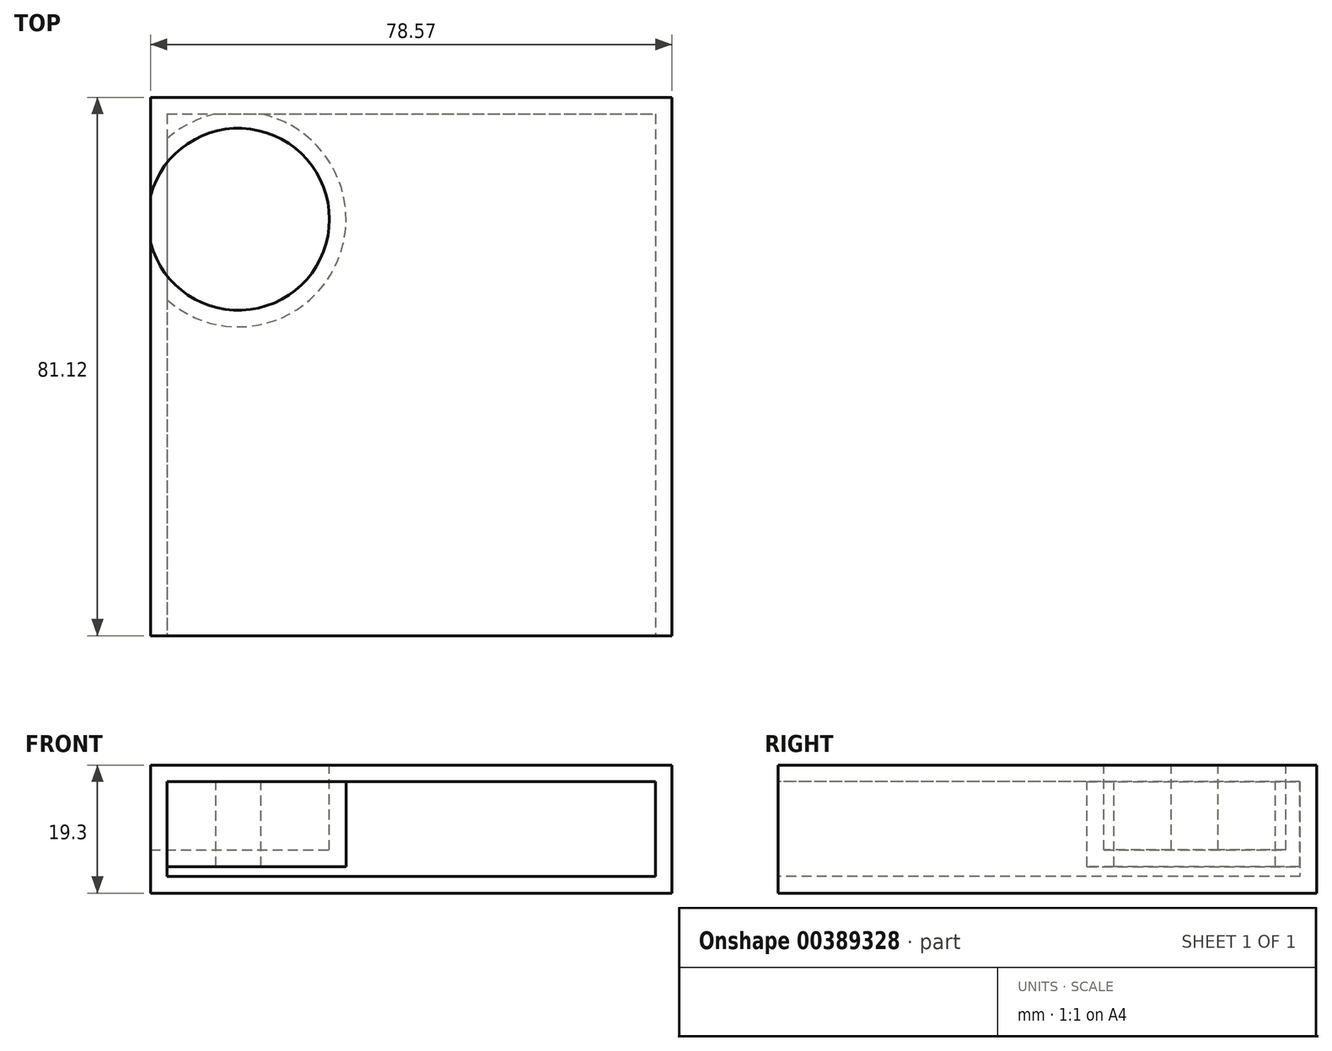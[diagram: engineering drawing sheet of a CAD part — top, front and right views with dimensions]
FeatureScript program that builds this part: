
annotation { "Feature Type Name" : "Feature", "Feature Type Description" : "" }
export const myFeature = defineFeature(function(context is Context, id is Id, definition is map)
    precondition{}
    {
        {
            var Q0;
            Q0=qCreatedBy(makeId("Top.planeOp"),FACE);
            var sketch = newSketch(context, id + "F0", { "sketchPlane" : qUnion([Q0])});
            skLineSegment(sketch, "E0.bottom", {"start": v(-38.35, 36.63) * mm, "end": v(40.22, 36.63) * mm});
            skLineSegment(sketch, "E0.top", {"start": v(-38.35, -33.82) * mm, "end": v(40.22, -33.82) * mm});
            skLineSegment(sketch, "E0.left", {"start": v(-38.35, 36.63) * mm, "end": v(-38.35, -33.82) * mm});
            skLineSegment(sketch, "E0.right", {"start": v(40.22, 36.63) * mm, "end": v(40.22, -33.82) * mm});
            skSolve(sketch);
        }
        {
            var Q0;
            Q0=makeQuery(id+"F0.imprint","IMPRINT",FACE,{"disambiguationData":[TD([[makeQuery(id+"F0.imprint","IMPRINT",EDGE,{"derivedFrom":sQuery(id+"F0.wireOp",EDGE,"E0.bottom")}),-1.0]])]});
            extrude(context, id + "F1", {"entities" : qUnion([Q0]), "depth" : 19.3 * mm});
        }
        {
            var Q0;
            Q0=makeQuery(id+"F1.opExtrude","SWEPT_FACE",FACE,{"disambiguationData":[OSD([sQuery(id+"F0.wireOp",EDGE,"E0.top")])]});
            extrude(context, id + "F2", {"entities" : qUnion([Q0]), "operationType" : NewBodyOperationType.ADD, "depth" : 10.67 * mm});
        }
        {
            var Q0;
            {var subQ0=sQuery(id+"F0.wireOp",EDGE,"E0.top");Q0=makeQuery(id+"F2.boolean.opBoolean","MERGE",FACE,{"derivedFrom":[makeQuery(id+"F1.opExtrude","CAP_FACE",FACE,{"disambiguationData":[OSD([sQuery(id+"F0.wireOp",EDGE,"E0.bottom"),subQ0,sQuery(id+"F0.wireOp",EDGE,"E0.left"),sQuery(id+"F0.wireOp",EDGE,"E0.right")])],"isStart":false}),makeQuery(id+"F2.opExtrude","SWEPT_FACE",FACE,{"disambiguationData":[OSD([subQ0]),TDD([makeQuery(id+"F1.opExtrude","CAP_EDGE",EDGE,{"disambiguationData":[OSD([subQ0])],"isStart":false})])]})]});}
            var sketch = newSketch(context, id + "F3", { "sketchPlane" : qUnion([Q0])});
            skSolve(sketch);
        }
        {
            var Q0;
            Q0=makeQuery(id+"F3.imprint","IMPRINT",FACE,{"disambiguationData":[TD([[makeQuery(id+"F3.imprint","IMPRINT",EDGE,{"derivedFrom":makeQuery(id+"F1.opExtrude","CAP_EDGE",EDGE,{"disambiguationData":[OSD([sQuery(id+"F0.wireOp",EDGE,"E0.bottom")])],"isStart":false})}),-1.0]])]});
            var sketch = newSketch(context, id + "F4", { "sketchPlane" : qUnion([Q0])});
            skCircle(sketch, "E1", {"center": v(-22.98, 0) * mm, "radius": 8.07 * mm});
            skSolve(sketch);
        }
        {
            var Q0;
            Q0=makeQuery(id+"F4.imprint","IMPRINT",FACE,{"disambiguationData":[TD([[makeQuery(id+"F4.imprint","IMPRINT",EDGE,{"derivedFrom":sQuery(id+"F4.wireOp",EDGE,"E1")}),1.0]])]});
            extrude(context, id + "F5", {"entities" : qUnion([Q0]), "operationType" : NewBodyOperationType.ADD, "oppositeDirection" : true, "depth" : 10.6 * mm});
        }
        {
            var Q0;
            Q0=makeQuery(id+"F3.imprint","IMPRINT",FACE,{"disambiguationData":[TD([[makeQuery(id+"F3.imprint","IMPRINT",EDGE,{"derivedFrom":makeQuery(id+"F1.opExtrude","CAP_EDGE",EDGE,{"disambiguationData":[OSD([sQuery(id+"F0.wireOp",EDGE,"E0.bottom")])],"isStart":false})}),-1.0]])]});
            var sketch = newSketch(context, id + "F6", { "sketchPlane" : qUnion([Q0])});
            skCircle(sketch, "E2", {"center": v(-25.1, 18.28) * mm, "radius": 13.71 * mm});
            skSolve(sketch);
        }
        {
            var Q0;
            {var subQ0=sQuery(id+"F6.wireOp",EDGE,"E2");var subQ1=sQuery(id+"F0.wireOp",EDGE,"E0.left");var subQ2=sQuery(id+"F0.wireOp",EDGE,"E0.top");var subQ3=makeQuery(id+"F3.imprint","IMPRINT",EDGE,{"derivedFrom":makeQuery(id+"F2.boolean.opBoolean","MERGE",EDGE,{"derivedFrom":[makeQuery(id+"F1.opExtrude","CAP_EDGE",EDGE,{"disambiguationData":[OSD([subQ1])],"isStart":false}),makeQuery(id+"F2.opExtrude","SWEPT_EDGE",EDGE,{"disambiguationData":[OSD([subQ2,subQ1]),TDD([makeQuery(id+"F1.opExtrude","CAP_VERTEX",VERTEX,{"disambiguationData":[OSD([subQ2,subQ1])],"isStart":false})])]})]})});var subQ4=makeQuery(id+"F6.imprint","INTERSECT",VERTEX,{"disambiguationData":[OD(0.0)],"derivedFrom":[subQ3,subQ0]});Q0=makeQuery(id+"F6.imprint","IMPRINT",FACE,{"disambiguationData":[TD([[makeQuery(id+"F6.imprint","IMPRINT",EDGE,{"disambiguationData":[TD([[subQ4,1.0]])],"derivedFrom":subQ0}),1.0]])]});}
            extrude(context, id + "F7", {"entities" : qUnion([Q0]), "operationType" : NewBodyOperationType.REMOVE, "oppositeDirection" : true, "depth" : 12.8 * mm});
        }
        {
            var Q0;
            Q0=makeQuery(id+"F2.opExtrude","CAP_FACE",FACE,{"disambiguationData":[OSD([sQuery(id+"F0.wireOp",EDGE,"E0.top")])],"isStart":false});
            shell(context, id + "F8", {"entities" : qUnion([Q0]), "thickness" : 2.5 * mm});
        }
    });
